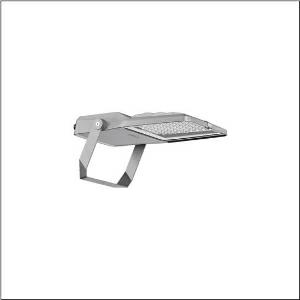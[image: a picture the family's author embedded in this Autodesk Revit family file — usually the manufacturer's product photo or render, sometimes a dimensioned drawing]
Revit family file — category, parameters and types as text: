
# Revit family: floodlight_fl_21_mini___pl43_5xa7772c1a1a_c7e6
name_source: partatom
category: Lighting Fixtures
units: mm (PartAtom-declared; Revit-internal decimal feet)

## family parameters
Cut with Voids When Loaded = No
Host = Face
Light Source = No
Part Type = Normal
Room Calculation Point = No
Round Connector Dimension = Use Diameter
Shared = No

## types (1)
- --- (1 x LED, 10370 lm, 87.2 W, 2200K)
    Apparent Load = 87 VA
    CIE Flux Codes = 27 78 99 100 100
    Color Rendering = 70
    Color Temperature = 2200K
    Default Elevation = 1800 mm
    Description = Floodlight FL 21 mini, floodlight, primary light control with lens, of PMMA, primary optical cover: protective disc, of toughened safety glass, transparent, light distribution: PL43, light emission: direct distribution, installation type: surface-mounted, LED, High Power LED, rated luminous flux: 10.370lm, luminous efficacy: 119lm/W, light colour: 722, colour temperature: 2200K, control gear: ECG iQ, control: Street-Remote, Auto-Match, Temp-Guard, Night-Set, Smart-Wire, Desk-Remote (wireless, voltage-free reading and setting of iQ features in the workshop via application-optimized NFC function/RFID function), optimised constant luminous flux control (CLO 2.0), with terminal, 6-pole, mains connection: 220..240V, AC, 50/60Hz, start of lifetime: 87W, end of lifetime: 92W, reduction: 40W, luminaire housing, of diecast aluminium, powder-coated, Siteco® metallic grey (DB 702S), corrosivity category C5 according to DIN EN ISO 12944, mounting bracket, of steel, galvanised, powder-coated, Siteco® metallic grey (DB 702S), protection rating (complete): IP66, insulation class (complete): insulation class II (safety insulation), certification: CE, ENEC, VDE, protection symbol: D, impact resistance: IK08, permissible operating ambient temperature: -40..+40°C, permissible operating ambient temperature for outdoor applications: -40..+50°C, standard: DIN EN 12944, packaging unit: 1 piece

Light Distribution: PL43
    Height = 70 mm
    Lamp = 1 x LED
    Lamp Light Flux = 10370 lm
    Lamp Power = 87.2 W
    Lamp count = 1
    Length = 485 mm
    Luminous efficacy = 119 lm/W
    Manufacturer = Siteco
    ModVariant = No
    Model = 5XA7772C1A1A
    Number of Poles = 1
    OnlyDefault = Yes
    Power Factor = 1
    Product Name = Floodlight FL 21 mini | PL43
    Product group = floodlight | pylon top
    ProductGroupID = 6101
    Protection Class = Protection class II
    Protection Degree = IP 66
    RLX_Detail_Level = 1
    RlxData = <blob elided: 95989 chars, md5=79365394>
    Socket = socket
    Standby Power = 0 W
    System Light Flux = 10370 lm
    System Power = 87 W
    Type Comments = factory setting: luminous flux: 100 % | dim-lin: 254 | 456 mA
    Type Image = l_1006845.jpg
    URL = http://relux.com
    VarID = @adj_073581
    Voltage = 0 V
    Weight = 0.00 kg
    Width = 337 mm

## geometry (parser evidence)
native form markers: Blend x4, Sweep x13
no freeform markers — native parametric forms only
